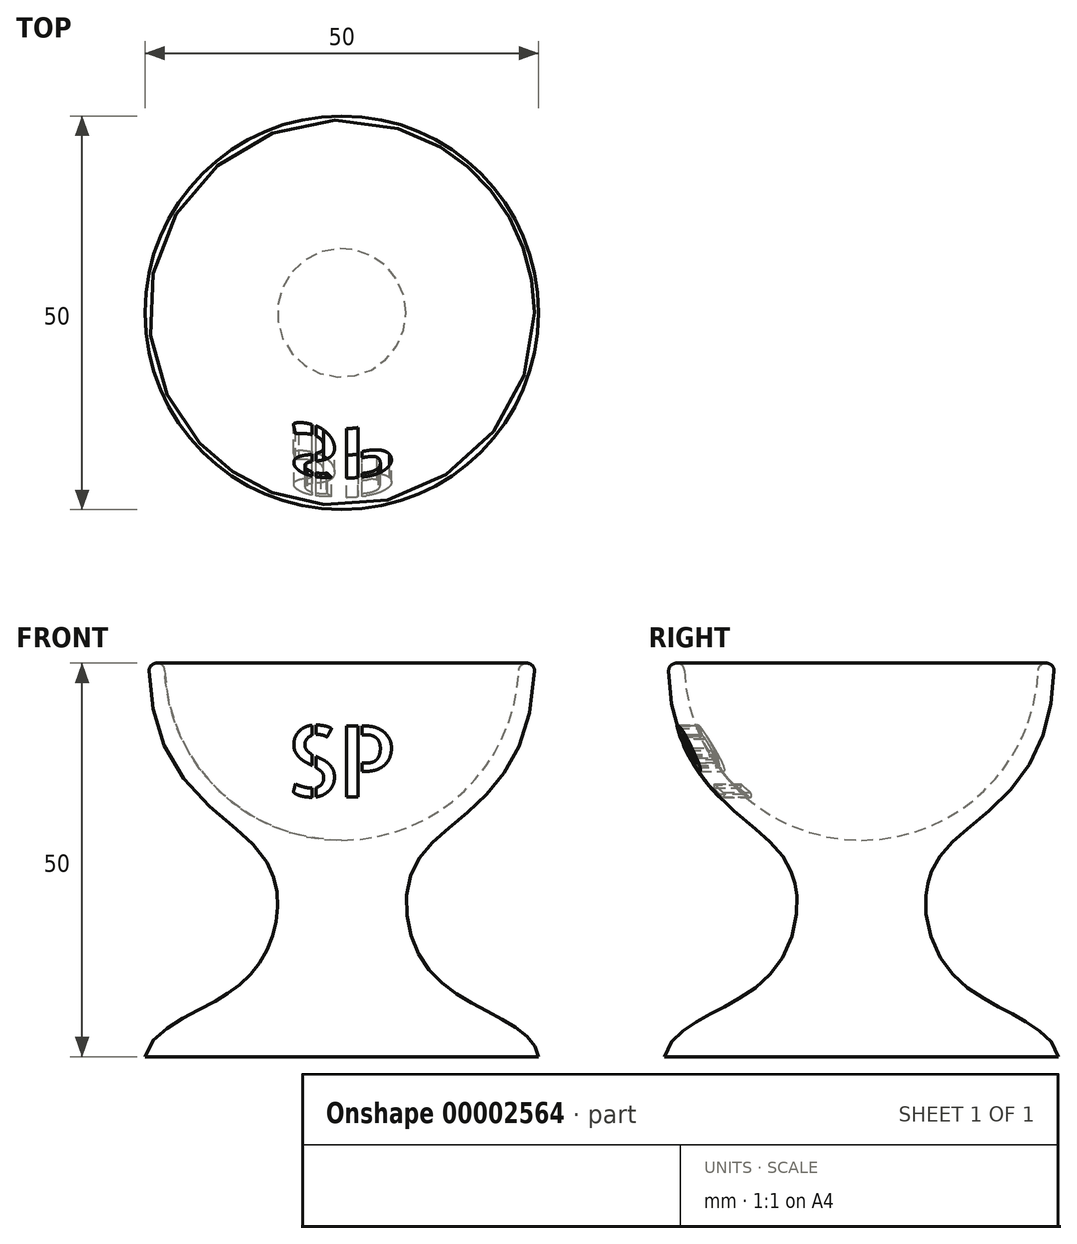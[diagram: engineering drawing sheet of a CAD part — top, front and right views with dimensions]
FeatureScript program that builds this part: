
annotation { "Feature Type Name" : "Feature", "Feature Type Description" : "" }
export const myFeature = defineFeature(function(context is Context, id is Id, definition is map)
    precondition{}
    {
        {
            var Q0;
            Q0=qCreatedBy(makeId("Front.planeOp"),FACE);
            var sketch = newSketch(context, id + "F0", { "sketchPlane" : qUnion([Q0])});
            skCircle(sketch, "E0", {"center": v(0, 50) * mm, "radius": 22.5 * mm});
            skLineSegment(sketch, "E1", {"start": v(0, 50) * mm, "end": v(0, 0) * mm});
            skFitSpline(sketch, "E2", {"points": [v(24.5, 50) * mm, v(9.62, 24.91) * mm, v(10.77, 11.44) * mm, v(20.54, 4.66) * mm, v(25, 0) * mm], "startDerivative": vector(-0.43, -141.75) * mm, "endDerivative": vector(4.3, -31.99) * mm});
            skLineSegment(sketch, "E3", {"start": v(24.5, 50) * mm, "end": v(0, 50) * mm});
            skLineSegment(sketch, "E4", {"start": v(25, 0) * mm, "end": v(0, 0) * mm});
            skSolve(sketch);
        }
        {
            var Q0;
            {var subQ1=sQuery(id+"F0.wireOp",EDGE,"E2");Q0=makeQuery(id+"F0.imprint","IMPRINT",FACE,{"disambiguationData":[TD([[makeQuery(id+"F0.imprint","IMPRINT",EDGE,{"derivedFrom":subQ1}),-1.0]])]});}
            var Q1;
            Q1=sQuery(id+"F0.wireOp",EDGE,"E1");
            revolve(context, id + "F1", {"entities" : qUnion([Q0]), "axis" : qUnion([Q1]), "revolveType" : RevolveType.FULL});
        }
        {
            var Q0;
            Q0=makeQuery(id+"F1.opRevolve","SWEPT_EDGE",EDGE,{"disambiguationData":[OSD([sQuery(id+"F0.wireOp",EDGE,"E2"),sQuery(id+"F0.wireOp",EDGE,"E3")])]});
            var Q1;
            Q1=makeQuery(id+"F1.opRevolve","SWEPT_EDGE",EDGE,{"disambiguationData":[OSD([sQuery(id+"F0.wireOp",EDGE,"E0"),sQuery(id+"F0.wireOp",EDGE,"E3")])]});
            fillet(context, id + "F2", {"entities" : qUnion([Q0, Q1]), "radius" : 1 * mm, "tangentPropagation" : true, "allowEdgeOverflow" : false});
        }
        {
            var Q0;
            Q0=qCreatedBy(makeId("Front.planeOp"),FACE);
            var sketch = newSketch(context, id + "F3", { "sketchPlane" : qUnion([Q0])});
            skText(sketch, "E5", { "text": "SP", "fontName": "AllertaStencil-Regular.ttf"});
            skLineSegment(sketch, "E6", {"start": v(0, 33) * mm, "end": v(0, 0) * mm, "construction": true});
            const initialGuessF3  = {"E5": [-0.00714, 0.033, 1, 0, 0.009]};
            skSetInitialGuess(sketch, initialGuessF3);
            skSolve(sketch);
        }
        {
            var Q0;
            Q0 = qSketchRegion(id + "F3", true);
            extrude(context, id + "F4", {"entities" : qUnion([Q0]), "operationType" : NewBodyOperationType.REMOVE, "depth" : 25 * mm});
        }
    });
